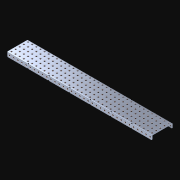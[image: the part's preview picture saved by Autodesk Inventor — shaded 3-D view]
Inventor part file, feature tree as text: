
AUTODESK INVENTOR PART (.ipt)
format: ipt  version: 2021 (Build 250183000, 183)  size: 2,485,760 bytes
history: native  units: in
note: dims shown in document units (in); Inventor stores cm internally (conversion verified against a paired STEP export)
features: other x246, extrude x245, pattern_linear x3, sketch x3
ambient origin geometry x8: Origin, YZ Plane, XZ Plane, XY Plane, X Axis, Y Axis, Z Axis, Center Point
bodies: Solid1 (feature_tree)
feature tree (497):
  pattern_linear  "Rectangular Pattern1"  Spacing1=0.046in  [1 undecoded]
  pattern_linear  "Rectangular Pattern2"  Spacing1=0.182in  [1 undecoded]
  pattern_linear  "Rectangular Pattern3"  Spacing1=0.046in  [1 undecoded]
  sketch  "Sketch1"  dims[d0=0.182in]
  other  "Srf1"
  sketch  "Sketch2"  dims[d1=0.046in d2=0.0in]
  other  "Srf2"
  sketch  "Sketch3"  dims[d3=0.182in d4=0.046in d5=0.0in d6=0.182in d7=0.046in d8=0.0in d11=0.5in d12=13.7795in d14=0.5in d15=1.9685in d17=0.5in d18=13.7795in d20=0.5in]
  other  "Srf3"
  other  "Srf4"
  other  "Srf5"
  other  "Srf6"
  other  "Srf7"
  other  "Srf8"
  other  "Srf9"
  other  "Srf10"
  other  "Srf11"
  other  "Srf12"
  other  "Srf13"
  other  "Srf14"
  other  "Srf15"
  other  "Srf16"
  other  "Srf17"
  other  "Srf18"
  other  "Srf19"
  other  "Srf20"
  other  "Srf21"
  other  "Srf22"
  other  "Srf23"
  other  "Srf24"
  other  "Srf25"
  other  "Srf26"
  other  "Srf27"
  other  "Srf28"
  other  "Srf29"
  other  "Srf30"
  other  "Srf31"
  other  "Srf32"
  other  "Srf33"
  other  "Srf34"
  other  "Srf35"
  other  "Srf36"
  other  "Srf37"
  other  "Srf38"
  other  "Srf39"
  other  "Srf40"
  other  "Srf41"
  other  "Srf42"
  other  "Srf43"
  other  "Srf44"
  other  "Srf45"
  other  "Srf46"
  other  "Srf47"
  other  "Srf48"
  other  "Srf49"
  other  "Srf50"
  other  "Srf51"
  other  "Srf52"
  other  "Srf53"
  other  "Srf54"
  other  "Srf55"
  other  "Srf56"
  other  "Srf57"
  other  "Srf58"
  other  "Srf59"
  other  "Srf60"
  other  "Srf61"
  other  "Srf62"
  other  "Srf63"
  other  "Srf64"
  other  "Srf65"
  other  "Srf66"
  other  "Srf67"
  other  "Srf68"
  other  "Srf69"
  other  "Srf70"
  other  "Srf71"
  other  "Srf72"
  other  "Srf73"
  other  "Srf74"
  other  "Srf75"
  other  "Srf76"
  other  "Srf77"
  other  "Srf78"
  other  "Srf79"
  other  "Srf80"
  other  "Srf81"
  other  "Srf82"
  other  "Srf83"
  other  "Srf84"
  other  "Srf85"
  other  "Srf86"
  other  "Srf87"
  other  "Srf88"
  other  "Srf89"
  other  "Srf90"
  other  "Srf91"
  other  "Srf92"
  other  "Srf93"
  other  "Srf94"
  other  "Srf95"
  other  "Srf96"
  other  "Srf97"
  other  "Srf98"
  other  "Srf99"
  other  "Srf100"
  other  "Srf101"
  other  "Srf102"
  other  "Srf103"
  other  "Srf104"
  other  "Srf105"
  other  "Srf106"
  other  "Srf107"
  other  "Srf108"
  other  "Srf109"
  other  "Srf110"
  other  "Srf111"
  other  "Srf112"
  other  "Srf113"
  other  "Srf114"
  other  "Srf115"
  other  "Srf116"
  other  "Srf117"
  other  "Srf118"
  other  "Srf119"
  other  "Srf120"
  other  "Srf121"
  other  "Srf122"
  other  "Srf123"
  other  "Srf124"
  other  "Srf125"
  other  "Srf126"
  other  "Srf127"
  other  "Srf128"
  other  "Srf129"
  other  "Srf130"
  other  "Srf131"
  other  "Srf132"
  other  "Srf133"
  other  "Srf134"
  other  "Srf135"
  other  "Srf136"
  other  "Srf137"
  other  "Srf138"
  other  "Srf139"
  other  "Srf140"
  other  "Srf141"
  other  "Srf142"
  other  "Srf143"
  other  "Srf144"
  other  "Srf145"
  other  "Srf146"
  other  "Srf147"
  other  "Srf148"
  other  "Srf149"
  other  "Srf150"
  other  "Srf151"
  other  "Srf152"
  other  "Srf153"
  other  "Srf154"
  other  "Srf155"
  other  "Srf156"
  other  "Srf157"
  other  "Srf158"
  other  "Srf159"
  other  "Srf160"
  other  "Srf161"
  other  "Srf162"
  other  "Srf163"
  other  "Srf164"
  other  "Srf165"
  other  "Srf166"
  other  "Srf167"
  other  "Srf168"
  other  "Srf169"
  other  "Srf170"
  other  "Srf171"
  other  "Srf172"
  other  "Srf173"
  other  "Srf174"
  other  "Srf175"
  other  "Srf176"
  other  "Srf177"
  other  "Srf178"
  other  "Srf179"
  other  "Srf180"
  other  "Srf181"
  other  "Srf182"
  other  "Srf183"
  other  "Srf184"
  other  "Srf185"
  other  "Srf186"
  other  "Srf187"
  other  "Srf188"
  other  "Srf189"
  other  "Srf190"
  other  "Srf191"
  other  "Srf192"
  other  "Srf193"
  other  "Srf194"
  other  "Srf195"
  other  "Srf196"
  other  "Srf197"
  other  "Srf198"
  other  "Srf199"
  other  "Srf200"
  other  "Srf201"
  other  "Srf202"
  other  "Srf203"
  other  "Srf204"
  other  "Srf205"
  other  "Srf206"
  other  "Srf207"
  other  "Srf208"
  other  "Srf209"
  other  "Srf210"
  other  "Srf211"
  other  "Srf212"
  other  "Srf213"
  other  "Srf214"
  other  "Srf215"
  other  "Srf216"
  other  "Srf217"
  other  "Srf218"
  other  "Srf219"
  other  "Srf220"
  other  "Srf221"
  other  "Srf222"
  other  "Srf223"
  other  "Srf224"
  other  "Srf225"
  other  "Srf226"
  other  "Srf227"
  other  "Srf228"
  other  "Srf229"
  other  "Srf230"
  other  "Srf231"
  other  "Srf232"
  other  "Srf233"
  other  "Srf234"
  other  "Srf235"
  other  "Srf236"
  other  "Srf237"
  other  "Srf238"
  other  "Srf239"
  other  "Srf240"
  other  "Srf241"
  other  "Srf242"
  other  "Srf243"
  other  "Srf244"
  other  "Srf245"
  parser-record x1  (decoder bookkeeping rows leaked as tree rows — omitted from the tree; the rows remain in map.json)
  extrude  "ExtrusionSrf1"  Depth=0.5in
  extrude  "ExtrusionSrf2"  Depth=0.5in
  extrude  "ExtrusionSrf3"  Depth=0.5in
  extrude  "ExtrusionSrf4"  Depth=0.5in
  extrude  "ExtrusionSrf5"  Depth=0.5in
  extrude  "ExtrusionSrf6"  Depth=0.5in
  extrude  "ExtrusionSrf7"  [1 undecoded]
  extrude  "ExtrusionSrf8"  [1 undecoded]
  extrude  "ExtrusionSrf9"  [1 undecoded]
  extrude  "ExtrusionSrf10"  [1 undecoded]
  extrude  "ExtrusionSrf11"  [1 undecoded]
  extrude  "ExtrusionSrf12"  [1 undecoded]
  extrude  "ExtrusionSrf13"  [1 undecoded]
  extrude  "ExtrusionSrf14"  [1 undecoded]
  extrude  "ExtrusionSrf15"  [1 undecoded]
  extrude  "ExtrusionSrf16"  [1 undecoded]
  extrude  "ExtrusionSrf17"  [1 undecoded]
  extrude  "ExtrusionSrf18"  [1 undecoded]
  extrude  "ExtrusionSrf19"  [1 undecoded]
  extrude  "ExtrusionSrf20"  [1 undecoded]
  extrude  "ExtrusionSrf21"  [1 undecoded]
  extrude  "ExtrusionSrf22"  [1 undecoded]
  extrude  "ExtrusionSrf23"  [1 undecoded]
  extrude  "ExtrusionSrf24"  [1 undecoded]
  extrude  "ExtrusionSrf25"  [1 undecoded]
  extrude  "ExtrusionSrf26"  [1 undecoded]
  extrude  "ExtrusionSrf27"  [1 undecoded]
  extrude  "ExtrusionSrf28"  [1 undecoded]
  extrude  "ExtrusionSrf29"  [1 undecoded]
  extrude  "ExtrusionSrf30"  [1 undecoded]
  extrude  "ExtrusionSrf31"  [1 undecoded]
  extrude  "ExtrusionSrf32"  [1 undecoded]
  extrude  "ExtrusionSrf33"  [1 undecoded]
  extrude  "ExtrusionSrf34"  [1 undecoded]
  extrude  "ExtrusionSrf35"  [1 undecoded]
  extrude  "ExtrusionSrf36"  [1 undecoded]
  extrude  "ExtrusionSrf37"  [1 undecoded]
  extrude  "ExtrusionSrf38"  [1 undecoded]
  extrude  "ExtrusionSrf39"  [1 undecoded]
  extrude  "ExtrusionSrf40"  [1 undecoded]
  extrude  "ExtrusionSrf41"  [1 undecoded]
  extrude  "ExtrusionSrf42"  [1 undecoded]
  extrude  "ExtrusionSrf43"  [1 undecoded]
  extrude  "ExtrusionSrf44"  [1 undecoded]
  extrude  "ExtrusionSrf45"  [1 undecoded]
  extrude  "ExtrusionSrf46"  [1 undecoded]
  extrude  "ExtrusionSrf47"  [1 undecoded]
  extrude  "ExtrusionSrf48"  [1 undecoded]
  extrude  "ExtrusionSrf49"  [1 undecoded]
  extrude  "ExtrusionSrf50"  [1 undecoded]
  extrude  "ExtrusionSrf51"  [1 undecoded]
  extrude  "ExtrusionSrf52"  [1 undecoded]
  extrude  "ExtrusionSrf53"  [1 undecoded]
  extrude  "ExtrusionSrf54"  [1 undecoded]
  extrude  "ExtrusionSrf55"  [1 undecoded]
  extrude  "ExtrusionSrf56"  [1 undecoded]
  extrude  "ExtrusionSrf57"  [1 undecoded]
  extrude  "ExtrusionSrf58"  [1 undecoded]
  extrude  "ExtrusionSrf59"  [1 undecoded]
  extrude  "ExtrusionSrf60"  [1 undecoded]
  extrude  "ExtrusionSrf61"  [1 undecoded]
  extrude  "ExtrusionSrf62"  [1 undecoded]
  extrude  "ExtrusionSrf63"  [1 undecoded]
  extrude  "ExtrusionSrf64"  [1 undecoded]
  extrude  "ExtrusionSrf65"  [1 undecoded]
  extrude  "ExtrusionSrf66"  [1 undecoded]
  extrude  "ExtrusionSrf67"  [1 undecoded]
  extrude  "ExtrusionSrf68"  [1 undecoded]
  extrude  "ExtrusionSrf69"  [1 undecoded]
  extrude  "ExtrusionSrf70"  [1 undecoded]
  extrude  "ExtrusionSrf71"  [1 undecoded]
  extrude  "ExtrusionSrf72"  [1 undecoded]
  extrude  "ExtrusionSrf73"  [1 undecoded]
  extrude  "ExtrusionSrf74"  [1 undecoded]
  extrude  "ExtrusionSrf75"  [1 undecoded]
  extrude  "ExtrusionSrf76"  [1 undecoded]
  extrude  "ExtrusionSrf77"  [1 undecoded]
  extrude  "ExtrusionSrf78"  [1 undecoded]
  extrude  "ExtrusionSrf79"  [1 undecoded]
  extrude  "ExtrusionSrf80"  [1 undecoded]
  extrude  "ExtrusionSrf81"  [1 undecoded]
  extrude  "ExtrusionSrf82"  [1 undecoded]
  extrude  "ExtrusionSrf83"  [1 undecoded]
  extrude  "ExtrusionSrf84"  [1 undecoded]
  extrude  "ExtrusionSrf85"  [1 undecoded]
  extrude  "ExtrusionSrf86"  [1 undecoded]
  extrude  "ExtrusionSrf87"  [1 undecoded]
  extrude  "ExtrusionSrf88"  [1 undecoded]
  extrude  "ExtrusionSrf89"  [1 undecoded]
  extrude  "ExtrusionSrf90"  [1 undecoded]
  extrude  "ExtrusionSrf91"  [1 undecoded]
  extrude  "ExtrusionSrf92"  [1 undecoded]
  extrude  "ExtrusionSrf93"  [1 undecoded]
  extrude  "ExtrusionSrf94"  [1 undecoded]
  extrude  "ExtrusionSrf95"  [1 undecoded]
  extrude  "ExtrusionSrf96"  [1 undecoded]
  extrude  "ExtrusionSrf97"  [1 undecoded]
  extrude  "ExtrusionSrf98"  [1 undecoded]
  extrude  "ExtrusionSrf99"  [1 undecoded]
  extrude  "ExtrusionSrf100"  [1 undecoded]
  extrude  "ExtrusionSrf101"  [1 undecoded]
  extrude  "ExtrusionSrf102"  [1 undecoded]
  extrude  "ExtrusionSrf103"  [1 undecoded]
  extrude  "ExtrusionSrf104"  [1 undecoded]
  extrude  "ExtrusionSrf105"  [1 undecoded]
  extrude  "ExtrusionSrf106"  [1 undecoded]
  extrude  "ExtrusionSrf107"  [1 undecoded]
  extrude  "ExtrusionSrf108"  [1 undecoded]
  extrude  "ExtrusionSrf109"  [1 undecoded]
  extrude  "ExtrusionSrf110"  [1 undecoded]
  extrude  "ExtrusionSrf111"  [1 undecoded]
  extrude  "ExtrusionSrf112"  [1 undecoded]
  extrude  "ExtrusionSrf113"  [1 undecoded]
  extrude  "ExtrusionSrf114"  [1 undecoded]
  extrude  "ExtrusionSrf115"  [1 undecoded]
  extrude  "ExtrusionSrf116"  [1 undecoded]
  extrude  "ExtrusionSrf117"  [1 undecoded]
  extrude  "ExtrusionSrf118"  [1 undecoded]
  extrude  "ExtrusionSrf119"  [1 undecoded]
  extrude  "ExtrusionSrf120"  [1 undecoded]
  extrude  "ExtrusionSrf121"  [1 undecoded]
  extrude  "ExtrusionSrf122"  [1 undecoded]
  extrude  "ExtrusionSrf123"  [1 undecoded]
  extrude  "ExtrusionSrf124"  [1 undecoded]
  extrude  "ExtrusionSrf125"  [1 undecoded]
  extrude  "ExtrusionSrf126"  [1 undecoded]
  extrude  "ExtrusionSrf127"  [1 undecoded]
  extrude  "ExtrusionSrf128"  [1 undecoded]
  extrude  "ExtrusionSrf129"  [1 undecoded]
  extrude  "ExtrusionSrf130"  [1 undecoded]
  extrude  "ExtrusionSrf131"  [1 undecoded]
  extrude  "ExtrusionSrf132"  [1 undecoded]
  extrude  "ExtrusionSrf133"  [1 undecoded]
  extrude  "ExtrusionSrf134"  [1 undecoded]
  extrude  "ExtrusionSrf135"  [1 undecoded]
  extrude  "ExtrusionSrf136"  [1 undecoded]
  extrude  "ExtrusionSrf137"  [1 undecoded]
  extrude  "ExtrusionSrf138"  [1 undecoded]
  extrude  "ExtrusionSrf139"  [1 undecoded]
  extrude  "ExtrusionSrf140"  [1 undecoded]
  extrude  "ExtrusionSrf141"  [1 undecoded]
  extrude  "ExtrusionSrf142"  [1 undecoded]
  extrude  "ExtrusionSrf143"  [1 undecoded]
  extrude  "ExtrusionSrf144"  [1 undecoded]
  extrude  "ExtrusionSrf145"  [1 undecoded]
  extrude  "ExtrusionSrf146"  [1 undecoded]
  extrude  "ExtrusionSrf147"  [1 undecoded]
  extrude  "ExtrusionSrf148"  [1 undecoded]
  extrude  "ExtrusionSrf149"  [1 undecoded]
  extrude  "ExtrusionSrf150"  [1 undecoded]
  extrude  "ExtrusionSrf151"  [1 undecoded]
  extrude  "ExtrusionSrf152"  [1 undecoded]
  extrude  "ExtrusionSrf153"  [1 undecoded]
  extrude  "ExtrusionSrf154"  [1 undecoded]
  extrude  "ExtrusionSrf155"  [1 undecoded]
  extrude  "ExtrusionSrf156"  [1 undecoded]
  extrude  "ExtrusionSrf157"  [1 undecoded]
  extrude  "ExtrusionSrf158"  [1 undecoded]
  extrude  "ExtrusionSrf159"  [1 undecoded]
  extrude  "ExtrusionSrf160"  [1 undecoded]
  extrude  "ExtrusionSrf161"  [1 undecoded]
  extrude  "ExtrusionSrf162"  [1 undecoded]
  extrude  "ExtrusionSrf163"  [1 undecoded]
  extrude  "ExtrusionSrf164"  [1 undecoded]
  extrude  "ExtrusionSrf165"  [1 undecoded]
  extrude  "ExtrusionSrf166"  [1 undecoded]
  extrude  "ExtrusionSrf167"  [1 undecoded]
  extrude  "ExtrusionSrf168"  [1 undecoded]
  extrude  "ExtrusionSrf169"  [1 undecoded]
  extrude  "ExtrusionSrf170"  [1 undecoded]
  extrude  "ExtrusionSrf171"  [1 undecoded]
  extrude  "ExtrusionSrf172"  [1 undecoded]
  extrude  "ExtrusionSrf173"  [1 undecoded]
  extrude  "ExtrusionSrf174"  [1 undecoded]
  extrude  "ExtrusionSrf175"  [1 undecoded]
  extrude  "ExtrusionSrf176"  [1 undecoded]
  extrude  "ExtrusionSrf177"  [1 undecoded]
  extrude  "ExtrusionSrf178"  [1 undecoded]
  extrude  "ExtrusionSrf179"  [1 undecoded]
  extrude  "ExtrusionSrf180"  [1 undecoded]
  extrude  "ExtrusionSrf181"  [1 undecoded]
  extrude  "ExtrusionSrf182"  [1 undecoded]
  extrude  "ExtrusionSrf183"  [1 undecoded]
  extrude  "ExtrusionSrf184"  [1 undecoded]
  extrude  "ExtrusionSrf185"  [1 undecoded]
  extrude  "ExtrusionSrf186"  [1 undecoded]
  extrude  "ExtrusionSrf187"  [1 undecoded]
  extrude  "ExtrusionSrf188"  [1 undecoded]
  extrude  "ExtrusionSrf189"  [1 undecoded]
  extrude  "ExtrusionSrf190"  [1 undecoded]
  extrude  "ExtrusionSrf191"  [1 undecoded]
  extrude  "ExtrusionSrf192"  [1 undecoded]
  extrude  "ExtrusionSrf193"  [1 undecoded]
  extrude  "ExtrusionSrf194"  [1 undecoded]
  extrude  "ExtrusionSrf195"  [1 undecoded]
  extrude  "ExtrusionSrf196"  [1 undecoded]
  extrude  "ExtrusionSrf197"  [1 undecoded]
  extrude  "ExtrusionSrf198"  [1 undecoded]
  extrude  "ExtrusionSrf199"  [1 undecoded]
  extrude  "ExtrusionSrf200"  [1 undecoded]
  extrude  "ExtrusionSrf201"  [1 undecoded]
  extrude  "ExtrusionSrf202"  [1 undecoded]
  extrude  "ExtrusionSrf203"  [1 undecoded]
  extrude  "ExtrusionSrf204"  [1 undecoded]
  extrude  "ExtrusionSrf205"  [1 undecoded]
  extrude  "ExtrusionSrf206"  [1 undecoded]
  extrude  "ExtrusionSrf207"  [1 undecoded]
  extrude  "ExtrusionSrf208"  [1 undecoded]
  extrude  "ExtrusionSrf209"  [1 undecoded]
  extrude  "ExtrusionSrf210"  [1 undecoded]
  extrude  "ExtrusionSrf211"  [1 undecoded]
  extrude  "ExtrusionSrf212"  [1 undecoded]
  extrude  "ExtrusionSrf213"  [1 undecoded]
  extrude  "ExtrusionSrf214"  [1 undecoded]
  extrude  "ExtrusionSrf215"  [1 undecoded]
  extrude  "ExtrusionSrf216"  [1 undecoded]
  extrude  "ExtrusionSrf217"  [1 undecoded]
  extrude  "ExtrusionSrf218"  [1 undecoded]
  extrude  "ExtrusionSrf219"  [1 undecoded]
  extrude  "ExtrusionSrf220"  [1 undecoded]
  extrude  "ExtrusionSrf221"  [1 undecoded]
  extrude  "ExtrusionSrf222"  [1 undecoded]
  extrude  "ExtrusionSrf223"  [1 undecoded]
  extrude  "ExtrusionSrf224"  [1 undecoded]
  extrude  "ExtrusionSrf225"  [1 undecoded]
  extrude  "ExtrusionSrf226"  [1 undecoded]
  extrude  "ExtrusionSrf227"  [1 undecoded]
  extrude  "ExtrusionSrf228"  [1 undecoded]
  extrude  "ExtrusionSrf229"  [1 undecoded]
  extrude  "ExtrusionSrf230"  [1 undecoded]
  extrude  "ExtrusionSrf231"  [1 undecoded]
  extrude  "ExtrusionSrf232"  [1 undecoded]
  extrude  "ExtrusionSrf233"  [1 undecoded]
  extrude  "ExtrusionSrf234"  [1 undecoded]
  extrude  "ExtrusionSrf235"  [1 undecoded]
  extrude  "ExtrusionSrf236"  [1 undecoded]
  extrude  "ExtrusionSrf237"  [1 undecoded]
  extrude  "ExtrusionSrf238"  [1 undecoded]
  extrude  "ExtrusionSrf239"  [1 undecoded]
  extrude  "ExtrusionSrf240"  [1 undecoded]
  extrude  "ExtrusionSrf241"  [1 undecoded]
  extrude  "ExtrusionSrf242"  [1 undecoded]
  extrude  "ExtrusionSrf243"  [1 undecoded]
  extrude  "ExtrusionSrf244"  [1 undecoded]
  extrude  "ExtrusionSrf245"  [1 undecoded]
note: 242 required parameter values undecoded (feature->parameter linkage not recoverable at this tier; creation-order binding heuristic only, values carry confidence <= 0.55)
